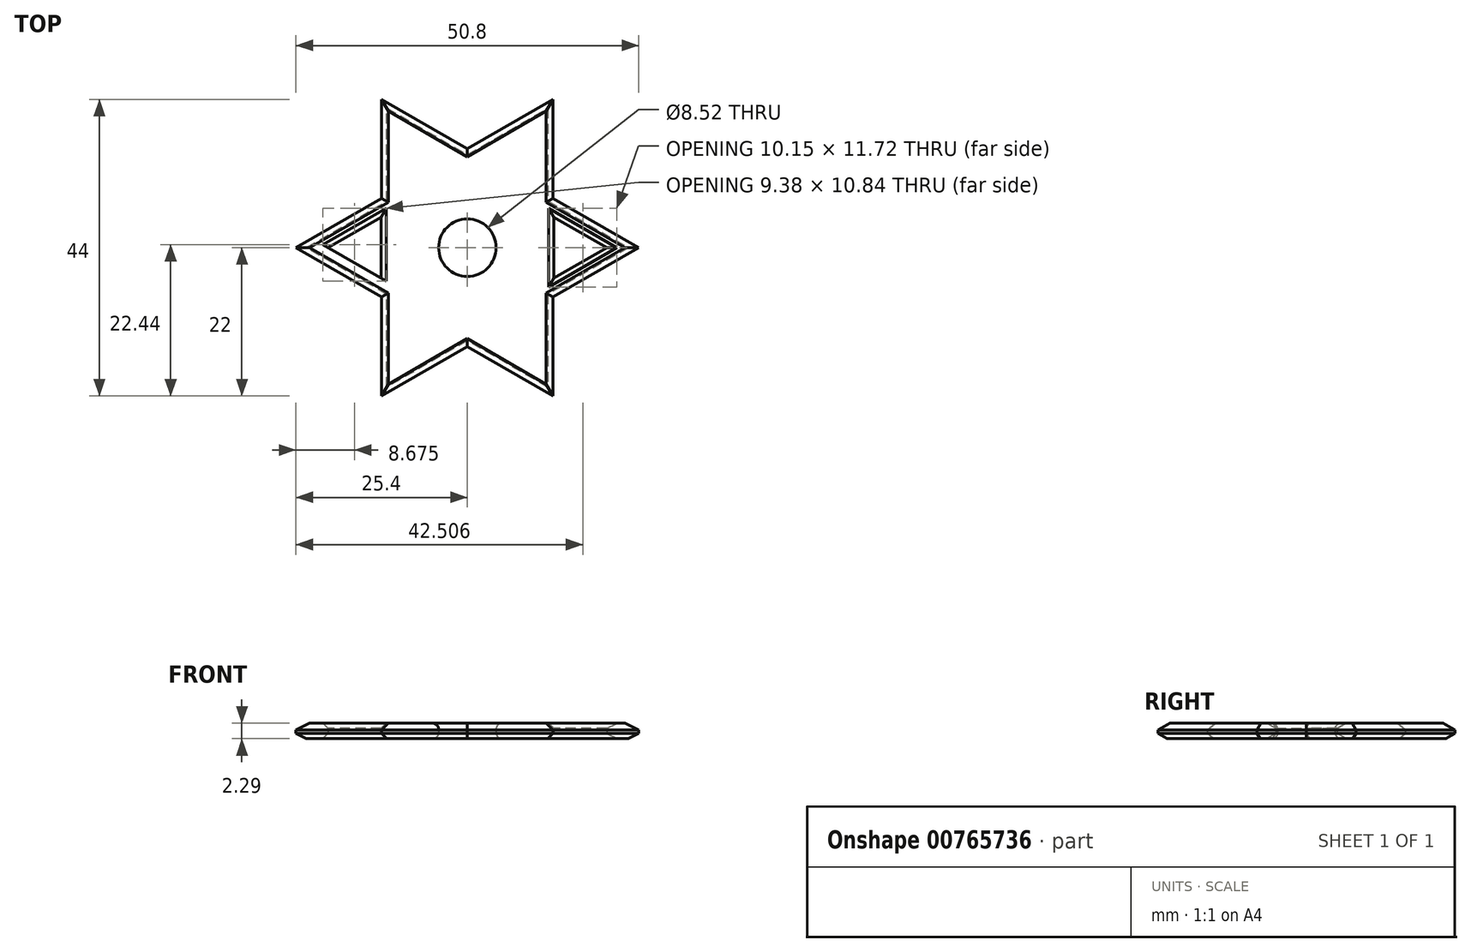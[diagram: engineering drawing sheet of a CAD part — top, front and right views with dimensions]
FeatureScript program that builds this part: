
annotation { "Feature Type Name" : "Feature", "Feature Type Description" : "" }
export const myFeature = defineFeature(function(context is Context, id is Id, definition is map)
    precondition{}
    {
        {
            var Q0;
            Q0=qCreatedBy(makeId("Top.planeOp"),FACE);
            var sketch = newSketch(context, id + "F0", { "sketchPlane" : qUnion([Q0])});
            skCircle(sketch, "E0.cCircle", {"center": v(0, 0) * mm, "radius": 12.7 * mm, "construction": true});
            skLineSegment(sketch, "E0.0", {"start": v(-12.7, 22) * mm, "end": v(25.4, 0) * mm});
            skLineSegment(sketch, "E0.1", {"start": v(25.4, 0) * mm, "end": v(-12.7, -22) * mm});
            skLineSegment(sketch, "E0.2", {"start": v(-12.7, -22) * mm, "end": v(-12.7, 22) * mm});
            skPoint(sketch, "E0.0.midPoint", {"position": v(6.35, 11) * mm});
            skLineSegment(sketch, "E1.0", {"start": v(12.7, 22) * mm, "end": v(12.7, -22) * mm});
            skLineSegment(sketch, "E1.1", {"start": v(12.7, -22) * mm, "end": v(-25.4, 0) * mm});
            skLineSegment(sketch, "E1.2", {"start": v(-25.4, 0) * mm, "end": v(12.7, 22) * mm});
            skPoint(sketch, "E1.0.midPoint", {"position": v(12.7, 0) * mm});
            skCircle(sketch, "E2", {"center": v(0, 0) * mm, "radius": 4.26 * mm});
            skCircle(sketch, "E3.cCircle", {"center": v(-15.42, 0) * mm, "radius": 2.62 * mm, "construction": true});
            skLineSegment(sketch, "E3.0", {"start": v(-12.8, 4.54) * mm, "end": v(-12.8, -4.54) * mm});
            skLineSegment(sketch, "E3.1", {"start": v(-12.8, -4.54) * mm, "end": v(-20.66, 0) * mm});
            skLineSegment(sketch, "E3.2", {"start": v(-20.66, 0) * mm, "end": v(-12.8, 4.54) * mm});
            skPoint(sketch, "E3.0.midPoint", {"position": v(-12.8, 0) * mm});
            skLineSegment(sketch, "E4.MirrorCS", {"start": v(12.8, 4.54) * mm, "end": v(12.8, -4.54) * mm});
            skLineSegment(sketch, "E5.MirrorCS", {"start": v(12.8, -4.54) * mm, "end": v(20.66, 0) * mm});
            skCircle(sketch, "E6.MirrorC", {"center": v(15.42, 0) * mm, "radius": 2.62 * mm, "construction": true});
            skLineSegment(sketch, "E7.MirrorCS", {"start": v(20.66, 0) * mm, "end": v(12.8, 4.54) * mm});
            skLineSegment(sketch, "E8.MirrorCS", {"start": v(-20.66, 0) * mm, "end": v(-12.8, -4.54) * mm});
            skSolve(sketch);
        }
        {
            var Q0;
            Q0 = qSketchRegion(id + "F0", true);
            extrude(context, id + "F1", {"entities" : qUnion([Q0]), "depth" : 2.3 * mm, "offsetDistance" : 25.4 * mm});
        }
        {
            var Q0;
            {var subQ0=sQuery(id+"F0.wireOp",EDGE,"E0.0");Q0=makeQuery(id+"F1.opExtrude","CAP_EDGE",EDGE,{"disambiguationData":[OSD([subQ0]),TDD([makeQuery(id+"F0.imprint","IMPRINT",EDGE,{"disambiguationData":[TD([[makeQuery(id+"F0.imprint","INTERSECT",VERTEX,{"derivedFrom":[subQ0,sQuery(id+"F0.wireOp",EDGE,"E0.2")]}),-1.0]])],"derivedFrom":subQ0})])],"isStart":false});}
            var Q1;
            {var subQ0=sQuery(id+"F0.wireOp",EDGE,"E0.2");Q1=makeQuery(id+"F1.opExtrude","CAP_EDGE",EDGE,{"disambiguationData":[OSD([subQ0]),TDD([makeQuery(id+"F0.imprint","IMPRINT",EDGE,{"disambiguationData":[TD([[makeQuery(id+"F0.imprint","INTERSECT",VERTEX,{"derivedFrom":[sQuery(id+"F0.wireOp",EDGE,"E0.0"),subQ0]}),1.0]])],"derivedFrom":subQ0})])],"isStart":false});}
            var Q2;
            {var subQ0=sQuery(id+"F0.wireOp",EDGE,"E1.2");Q2=makeQuery(id+"F1.opExtrude","CAP_EDGE",EDGE,{"disambiguationData":[OSD([subQ0]),TDD([makeQuery(id+"F0.imprint","IMPRINT",EDGE,{"disambiguationData":[TD([[makeQuery(id+"F0.imprint","INTERSECT",VERTEX,{"derivedFrom":[sQuery(id+"F0.wireOp",EDGE,"E1.1"),subQ0]}),-1.0]])],"derivedFrom":subQ0})])],"isStart":false});}
            var Q3;
            {var subQ0=sQuery(id+"F0.wireOp",EDGE,"E1.1");Q3=makeQuery(id+"F1.opExtrude","CAP_EDGE",EDGE,{"disambiguationData":[OSD([subQ0]),TDD([makeQuery(id+"F0.imprint","IMPRINT",EDGE,{"disambiguationData":[TD([[makeQuery(id+"F0.imprint","INTERSECT",VERTEX,{"derivedFrom":[subQ0,sQuery(id+"F0.wireOp",EDGE,"E1.2")]}),1.0]])],"derivedFrom":subQ0})])],"isStart":false});}
            var Q4;
            {var subQ0=sQuery(id+"F0.wireOp",EDGE,"E0.2");Q4=makeQuery(id+"F1.opExtrude","CAP_EDGE",EDGE,{"disambiguationData":[OSD([subQ0]),TDD([makeQuery(id+"F0.imprint","IMPRINT",EDGE,{"disambiguationData":[TD([[makeQuery(id+"F0.imprint","INTERSECT",VERTEX,{"derivedFrom":[sQuery(id+"F0.wireOp",EDGE,"E0.1"),subQ0]}),-1.0]])],"derivedFrom":subQ0})])],"isStart":false});}
            var Q5;
            {var subQ0=sQuery(id+"F0.wireOp",EDGE,"E0.1");Q5=makeQuery(id+"F1.opExtrude","CAP_EDGE",EDGE,{"disambiguationData":[OSD([subQ0]),TDD([makeQuery(id+"F0.imprint","IMPRINT",EDGE,{"disambiguationData":[TD([[makeQuery(id+"F0.imprint","INTERSECT",VERTEX,{"derivedFrom":[subQ0,sQuery(id+"F0.wireOp",EDGE,"E0.2")]}),1.0]])],"derivedFrom":subQ0})])],"isStart":false});}
            var Q6;
            {var subQ0=sQuery(id+"F0.wireOp",EDGE,"E1.1");Q6=makeQuery(id+"F1.opExtrude","CAP_EDGE",EDGE,{"disambiguationData":[OSD([subQ0]),TDD([makeQuery(id+"F0.imprint","IMPRINT",EDGE,{"disambiguationData":[TD([[makeQuery(id+"F0.imprint","INTERSECT",VERTEX,{"derivedFrom":[sQuery(id+"F0.wireOp",EDGE,"E1.0"),subQ0]}),-1.0]])],"derivedFrom":subQ0})])],"isStart":false});}
            var Q7;
            {var subQ0=sQuery(id+"F0.wireOp",EDGE,"E1.0");Q7=makeQuery(id+"F1.opExtrude","CAP_EDGE",EDGE,{"disambiguationData":[OSD([subQ0]),TDD([makeQuery(id+"F0.imprint","IMPRINT",EDGE,{"disambiguationData":[TD([[makeQuery(id+"F0.imprint","INTERSECT",VERTEX,{"derivedFrom":[subQ0,sQuery(id+"F0.wireOp",EDGE,"E1.1")]}),1.0]])],"derivedFrom":subQ0})])],"isStart":false});}
            var Q8;
            {var subQ0=sQuery(id+"F0.wireOp",EDGE,"E0.1");Q8=makeQuery(id+"F1.opExtrude","CAP_EDGE",EDGE,{"disambiguationData":[OSD([subQ0]),TDD([makeQuery(id+"F0.imprint","IMPRINT",EDGE,{"disambiguationData":[TD([[makeQuery(id+"F0.imprint","INTERSECT",VERTEX,{"derivedFrom":[sQuery(id+"F0.wireOp",EDGE,"E0.0"),subQ0]}),-1.0]])],"derivedFrom":subQ0})])],"isStart":false});}
            var Q9;
            {var subQ0=sQuery(id+"F0.wireOp",EDGE,"E0.0");Q9=makeQuery(id+"F1.opExtrude","CAP_EDGE",EDGE,{"disambiguationData":[OSD([subQ0]),TDD([makeQuery(id+"F0.imprint","IMPRINT",EDGE,{"disambiguationData":[TD([[makeQuery(id+"F0.imprint","INTERSECT",VERTEX,{"derivedFrom":[subQ0,sQuery(id+"F0.wireOp",EDGE,"E0.1")]}),1.0]])],"derivedFrom":subQ0})])],"isStart":false});}
            var Q10;
            {var subQ0=sQuery(id+"F0.wireOp",EDGE,"E1.0");Q10=makeQuery(id+"F1.opExtrude","CAP_EDGE",EDGE,{"disambiguationData":[OSD([subQ0]),TDD([makeQuery(id+"F0.imprint","IMPRINT",EDGE,{"disambiguationData":[TD([[makeQuery(id+"F0.imprint","INTERSECT",VERTEX,{"derivedFrom":[subQ0,sQuery(id+"F0.wireOp",EDGE,"E1.2")]}),-1.0]])],"derivedFrom":subQ0})])],"isStart":false});}
            var Q11;
            {var subQ0=sQuery(id+"F0.wireOp",EDGE,"E1.2");Q11=makeQuery(id+"F1.opExtrude","CAP_EDGE",EDGE,{"disambiguationData":[OSD([subQ0]),TDD([makeQuery(id+"F0.imprint","IMPRINT",EDGE,{"disambiguationData":[TD([[makeQuery(id+"F0.imprint","INTERSECT",VERTEX,{"derivedFrom":[sQuery(id+"F0.wireOp",EDGE,"E1.0"),subQ0]}),1.0]])],"derivedFrom":subQ0})])],"isStart":false});}
            chamfer(context, id + "F2", {"entities" : qUnion([Q0, Q1, Q2, Q3, Q4, Q5, Q6, Q7, Q8, Q9, Q10, Q11]), "width" : 1.02 * mm, "tangentPropagation" : true});
        }
        {
            var Q0;
            Q0=makeQuery(id+"F1.opExtrude","CAP_EDGE",EDGE,{"disambiguationData":[OSD([sQuery(id+"F0.wireOp",EDGE,"E2")])],"isStart":true});
            var Q1;
            Q1=makeQuery(id+"F1.opExtrude","CAP_EDGE",EDGE,{"disambiguationData":[OSD([sQuery(id+"F0.wireOp",EDGE,"E2")])],"isStart":false});
            fillet(context, id + "F3", {"entities" : qUnion([Q0, Q1]), "radius" : 0.89 * mm, "tangentPropagation" : true, "allowEdgeOverflow" : false});
        }
        {
            var Q0;
            {var subQ0=sQuery(id+"F0.wireOp",EDGE,"E0.1");Q0=makeQuery(id+"F1.opExtrude","CAP_EDGE",EDGE,{"disambiguationData":[OSD([subQ0]),TDD([makeQuery(id+"F0.imprint","IMPRINT",EDGE,{"disambiguationData":[TD([[makeQuery(id+"F0.imprint","INTERSECT",VERTEX,{"derivedFrom":[subQ0,sQuery(id+"F0.wireOp",EDGE,"E0.2")]}),1.0]])],"derivedFrom":subQ0})])],"isStart":true});}
            var Q1;
            {var subQ0=sQuery(id+"F0.wireOp",EDGE,"E1.1");Q1=makeQuery(id+"F1.opExtrude","CAP_EDGE",EDGE,{"disambiguationData":[OSD([subQ0]),TDD([makeQuery(id+"F0.imprint","IMPRINT",EDGE,{"disambiguationData":[TD([[makeQuery(id+"F0.imprint","INTERSECT",VERTEX,{"derivedFrom":[sQuery(id+"F0.wireOp",EDGE,"E1.0"),subQ0]}),-1.0]])],"derivedFrom":subQ0})])],"isStart":true});}
            var Q2;
            {var subQ0=sQuery(id+"F0.wireOp",EDGE,"E1.0");Q2=makeQuery(id+"F1.opExtrude","CAP_EDGE",EDGE,{"disambiguationData":[OSD([subQ0]),TDD([makeQuery(id+"F0.imprint","IMPRINT",EDGE,{"disambiguationData":[TD([[makeQuery(id+"F0.imprint","INTERSECT",VERTEX,{"derivedFrom":[subQ0,sQuery(id+"F0.wireOp",EDGE,"E1.1")]}),1.0]])],"derivedFrom":subQ0})])],"isStart":true});}
            var Q3;
            {var subQ0=sQuery(id+"F0.wireOp",EDGE,"E0.1");Q3=makeQuery(id+"F1.opExtrude","CAP_EDGE",EDGE,{"disambiguationData":[OSD([subQ0]),TDD([makeQuery(id+"F0.imprint","IMPRINT",EDGE,{"disambiguationData":[TD([[makeQuery(id+"F0.imprint","INTERSECT",VERTEX,{"derivedFrom":[sQuery(id+"F0.wireOp",EDGE,"E0.0"),subQ0]}),-1.0]])],"derivedFrom":subQ0})])],"isStart":true});}
            var Q4;
            {var subQ0=sQuery(id+"F0.wireOp",EDGE,"E0.0");Q4=makeQuery(id+"F1.opExtrude","CAP_EDGE",EDGE,{"disambiguationData":[OSD([subQ0]),TDD([makeQuery(id+"F0.imprint","IMPRINT",EDGE,{"disambiguationData":[TD([[makeQuery(id+"F0.imprint","INTERSECT",VERTEX,{"derivedFrom":[subQ0,sQuery(id+"F0.wireOp",EDGE,"E0.1")]}),1.0]])],"derivedFrom":subQ0})])],"isStart":true});}
            var Q5;
            {var subQ0=sQuery(id+"F0.wireOp",EDGE,"E1.0");Q5=makeQuery(id+"F1.opExtrude","CAP_EDGE",EDGE,{"disambiguationData":[OSD([subQ0]),TDD([makeQuery(id+"F0.imprint","IMPRINT",EDGE,{"disambiguationData":[TD([[makeQuery(id+"F0.imprint","INTERSECT",VERTEX,{"derivedFrom":[subQ0,sQuery(id+"F0.wireOp",EDGE,"E1.2")]}),-1.0]])],"derivedFrom":subQ0})])],"isStart":true});}
            var Q6;
            {var subQ0=sQuery(id+"F0.wireOp",EDGE,"E1.2");Q6=makeQuery(id+"F1.opExtrude","CAP_EDGE",EDGE,{"disambiguationData":[OSD([subQ0]),TDD([makeQuery(id+"F0.imprint","IMPRINT",EDGE,{"disambiguationData":[TD([[makeQuery(id+"F0.imprint","INTERSECT",VERTEX,{"derivedFrom":[sQuery(id+"F0.wireOp",EDGE,"E1.0"),subQ0]}),1.0]])],"derivedFrom":subQ0})])],"isStart":true});}
            var Q7;
            {var subQ0=sQuery(id+"F0.wireOp",EDGE,"E0.0");Q7=makeQuery(id+"F1.opExtrude","CAP_EDGE",EDGE,{"disambiguationData":[OSD([subQ0]),TDD([makeQuery(id+"F0.imprint","IMPRINT",EDGE,{"disambiguationData":[TD([[makeQuery(id+"F0.imprint","INTERSECT",VERTEX,{"derivedFrom":[subQ0,sQuery(id+"F0.wireOp",EDGE,"E0.2")]}),-1.0]])],"derivedFrom":subQ0})])],"isStart":true});}
            var Q8;
            {var subQ0=sQuery(id+"F0.wireOp",EDGE,"E0.2");Q8=makeQuery(id+"F1.opExtrude","CAP_EDGE",EDGE,{"disambiguationData":[OSD([subQ0]),TDD([makeQuery(id+"F0.imprint","IMPRINT",EDGE,{"disambiguationData":[TD([[makeQuery(id+"F0.imprint","INTERSECT",VERTEX,{"derivedFrom":[sQuery(id+"F0.wireOp",EDGE,"E0.0"),subQ0]}),1.0]])],"derivedFrom":subQ0})])],"isStart":true});}
            var Q9;
            {var subQ0=sQuery(id+"F0.wireOp",EDGE,"E1.2");Q9=makeQuery(id+"F1.opExtrude","CAP_EDGE",EDGE,{"disambiguationData":[OSD([subQ0]),TDD([makeQuery(id+"F0.imprint","IMPRINT",EDGE,{"disambiguationData":[TD([[makeQuery(id+"F0.imprint","INTERSECT",VERTEX,{"derivedFrom":[sQuery(id+"F0.wireOp",EDGE,"E1.1"),subQ0]}),-1.0]])],"derivedFrom":subQ0})])],"isStart":true});}
            var Q10;
            {var subQ0=sQuery(id+"F0.wireOp",EDGE,"E1.1");Q10=makeQuery(id+"F1.opExtrude","CAP_EDGE",EDGE,{"disambiguationData":[OSD([subQ0]),TDD([makeQuery(id+"F0.imprint","IMPRINT",EDGE,{"disambiguationData":[TD([[makeQuery(id+"F0.imprint","INTERSECT",VERTEX,{"derivedFrom":[subQ0,sQuery(id+"F0.wireOp",EDGE,"E1.2")]}),1.0]])],"derivedFrom":subQ0})])],"isStart":true});}
            var Q11;
            {var subQ0=sQuery(id+"F0.wireOp",EDGE,"E0.2");Q11=makeQuery(id+"F1.opExtrude","CAP_EDGE",EDGE,{"disambiguationData":[OSD([subQ0]),TDD([makeQuery(id+"F0.imprint","IMPRINT",EDGE,{"disambiguationData":[TD([[makeQuery(id+"F0.imprint","INTERSECT",VERTEX,{"derivedFrom":[sQuery(id+"F0.wireOp",EDGE,"E0.1"),subQ0]}),-1.0]])],"derivedFrom":subQ0})])],"isStart":true});}
            chamfer(context, id + "F4", {"entities" : qUnion([Q0, Q1, Q2, Q3, Q4, Q5, Q6, Q7, Q8, Q9, Q10, Q11]), "width" : 0.76 * mm, "tangentPropagation" : true});
        }
        {
            var Q0;
            Q0=makeQuery(id+"F1.opExtrude","CAP_EDGE",EDGE,{"disambiguationData":[OSD([sQuery(id+"F0.wireOp",EDGE,"E3.2")])],"isStart":false});
            var Q1;
            Q1=makeQuery(id+"F1.opExtrude","CAP_EDGE",EDGE,{"disambiguationData":[OSD([sQuery(id+"F0.wireOp",EDGE,"E3.0")])],"isStart":false});
            var Q2;
            Q2=makeQuery(id+"F1.opExtrude","CAP_EDGE",EDGE,{"disambiguationData":[OSD([sQuery(id+"F0.wireOp",EDGE,"E8.MirrorCS")])],"isStart":false});
            var Q3;
            Q3=makeQuery(id+"F1.opExtrude","CAP_EDGE",EDGE,{"disambiguationData":[OSD([sQuery(id+"F0.wireOp",EDGE,"E4.MirrorCS")])],"isStart":false});
            var Q4;
            Q4=makeQuery(id+"F1.opExtrude","CAP_EDGE",EDGE,{"disambiguationData":[OSD([sQuery(id+"F0.wireOp",EDGE,"E7.MirrorCS")])],"isStart":false});
            var Q5;
            Q5=makeQuery(id+"F1.opExtrude","CAP_EDGE",EDGE,{"disambiguationData":[OSD([sQuery(id+"F0.wireOp",EDGE,"E5.MirrorCS")])],"isStart":false});
            var Q6;
            Q6=makeQuery(id+"F1.opExtrude","CAP_EDGE",EDGE,{"disambiguationData":[OSD([sQuery(id+"F0.wireOp",EDGE,"E7.MirrorCS")])],"isStart":true});
            var Q7;
            Q7=makeQuery(id+"F1.opExtrude","CAP_EDGE",EDGE,{"disambiguationData":[OSD([sQuery(id+"F0.wireOp",EDGE,"E4.MirrorCS")])],"isStart":true});
            var Q8;
            Q8=makeQuery(id+"F1.opExtrude","CAP_EDGE",EDGE,{"disambiguationData":[OSD([sQuery(id+"F0.wireOp",EDGE,"E5.MirrorCS")])],"isStart":true});
            var Q9;
            Q9=makeQuery(id+"F1.opExtrude","CAP_EDGE",EDGE,{"disambiguationData":[OSD([sQuery(id+"F0.wireOp",EDGE,"E3.2")])],"isStart":true});
            var Q10;
            Q10=makeQuery(id+"F1.opExtrude","CAP_EDGE",EDGE,{"disambiguationData":[OSD([sQuery(id+"F0.wireOp",EDGE,"E8.MirrorCS")])],"isStart":true});
            var Q11;
            Q11=makeQuery(id+"F1.opExtrude","CAP_EDGE",EDGE,{"disambiguationData":[OSD([sQuery(id+"F0.wireOp",EDGE,"E3.0")])],"isStart":true});
            chamfer(context, id + "F5", {"entities" : qUnion([Q0, Q1, Q2, Q3, Q4, Q5, Q6, Q7, Q8, Q9, Q10, Q11]), "width" : 0.76 * mm, "tangentPropagation" : true});
        }
    });
